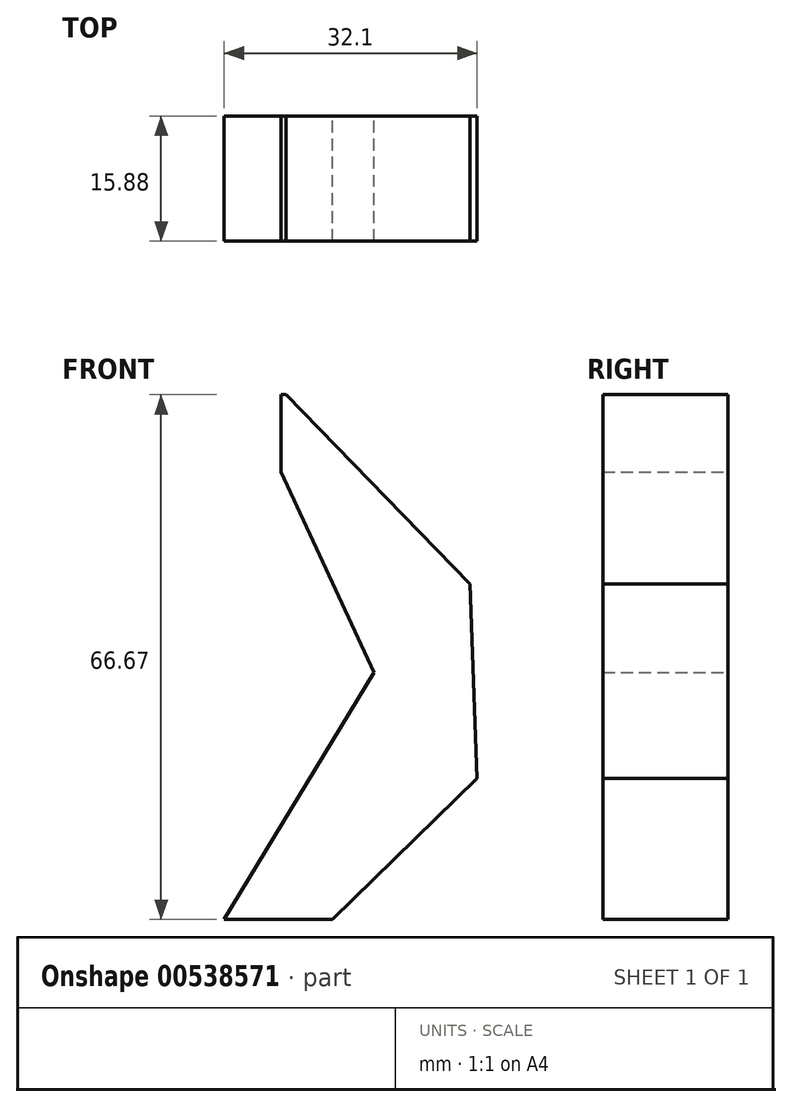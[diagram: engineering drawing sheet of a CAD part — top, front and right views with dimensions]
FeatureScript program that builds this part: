
annotation { "Feature Type Name" : "Feature", "Feature Type Description" : "" }
export const myFeature = defineFeature(function(context is Context, id is Id, definition is map)
    precondition{}
    {
        {
            var Q0;
            Q0=qCreatedBy(makeId("Front.planeOp"),FACE);
            var sketch = newSketch(context, id + "F0", { "sketchPlane" : qUnion([Q0])});
            skLineSegment(sketch, "E0", {"start": v(-19.05, 31.4) * mm, "end": v(-19.05, 31.4) * mm});
            skLineSegment(sketch, "E1.MirrorCS", {"start": v(7.22, 56.8) * mm, "end": v(19.05, 31.4) * mm});
            skLineSegment(sketch, "E2.MirrorCS", {"start": v(7.22, 66.67) * mm, "end": v(7.22, 56.8) * mm});
            skLineSegment(sketch, "E3.MirrorCS", {"start": v(7.87, 66.67) * mm, "end": v(7.22, 66.67) * mm});
            skLineSegment(sketch, "E4.MirrorCS", {"start": v(7.87, 66.67) * mm, "end": v(31.22, 42.62) * mm});
            skLineSegment(sketch, "E5.MirrorCS", {"start": v(31.22, 42.62) * mm, "end": v(32.1, 17.9) * mm});
            skLineSegment(sketch, "E6.MirrorCS", {"start": v(13.72, 0) * mm, "end": v(32.1, 17.9) * mm});
            skLineSegment(sketch, "E7.MirrorCS", {"start": v(13.72, 0) * mm, "end": v(10.88, -58.12) * mm});
            skLineSegment(sketch, "E8.MirrorCS", {"start": v(19.05, 31.4) * mm, "end": v(0, 0) * mm});
            skLineSegment(sketch, "E9.MirrorCS", {"start": v(19.05, 31.4) * mm, "end": v(19.05, 31.4) * mm});
            skPoint(sketch, "E10.orphan", {"position": v(30.37, 66.67) * mm});
            skPoint(sketch, "E11.orphan", {"position": v(34.79, -58.04) * mm});
            skPoint(sketch, "E12.orphan", {"position": v(-34.79, -58.04) * mm});
            skPoint(sketch, "E13.orphan", {"position": v(-30.37, 66.67) * mm});
            skPoint(sketch, "E14.center.orphan", {"position": v(0, -8.6) * mm});
            skPoint(sketch, "E15.trimOffspring.end.orphan", {"position": v(7.22, -58.12) * mm});
            skPoint(sketch, "E16.top.end.orphan", {"position": v(-7.22, -58.12) * mm});
            skPoint(sketch, "E17.end.orphan", {"position": v(0, 0) * mm});
            skPoint(sketch, "E16.right.end.orphan", {"position": v(-7.22, 56.8) * mm});
            skPoint(sketch, "E16.left.start.orphan", {"position": v(-31.22, 42.62) * mm});
            skPoint(sketch, "E16.bottom.end.orphan", {"position": v(-7.22, 66.67) * mm});
            skPoint(sketch, "E16.bottom.start.orphan", {"position": v(-7.87, 66.67) * mm});
            skPoint(sketch, "E18.end.orphan", {"position": v(-32.1, 17.9) * mm});
            skPoint(sketch, "E19.end.orphan", {"position": v(-10.88, -58.12) * mm});
            skPoint(sketch, "E19.start.orphan", {"position": v(-13.72, 0) * mm});
            skLineSegment(sketch, "E20", {"start": v(0, 0) * mm, "end": v(10.88, -58.12) * mm});
            skLineSegment(sketch, "E21", {"start": v(0, 0) * mm, "end": v(13.72, 0) * mm});
            skSolve(sketch);
        }
        {
            var Q0;
            Q0=makeQuery(id+"F0.imprint","IMPRINT",FACE,{"disambiguationData":[TD([[makeQuery(id+"F0.imprint","IMPRINT",EDGE,{"derivedFrom":sQuery(id+"F0.wireOp",EDGE,"E1.MirrorCS")}),1.0]])]});
            extrude(context, id + "F1", {"entities" : qUnion([Q0]), "depth" : 15.88 * mm, "offsetDistance" : 25.4 * mm});
        }
    });
